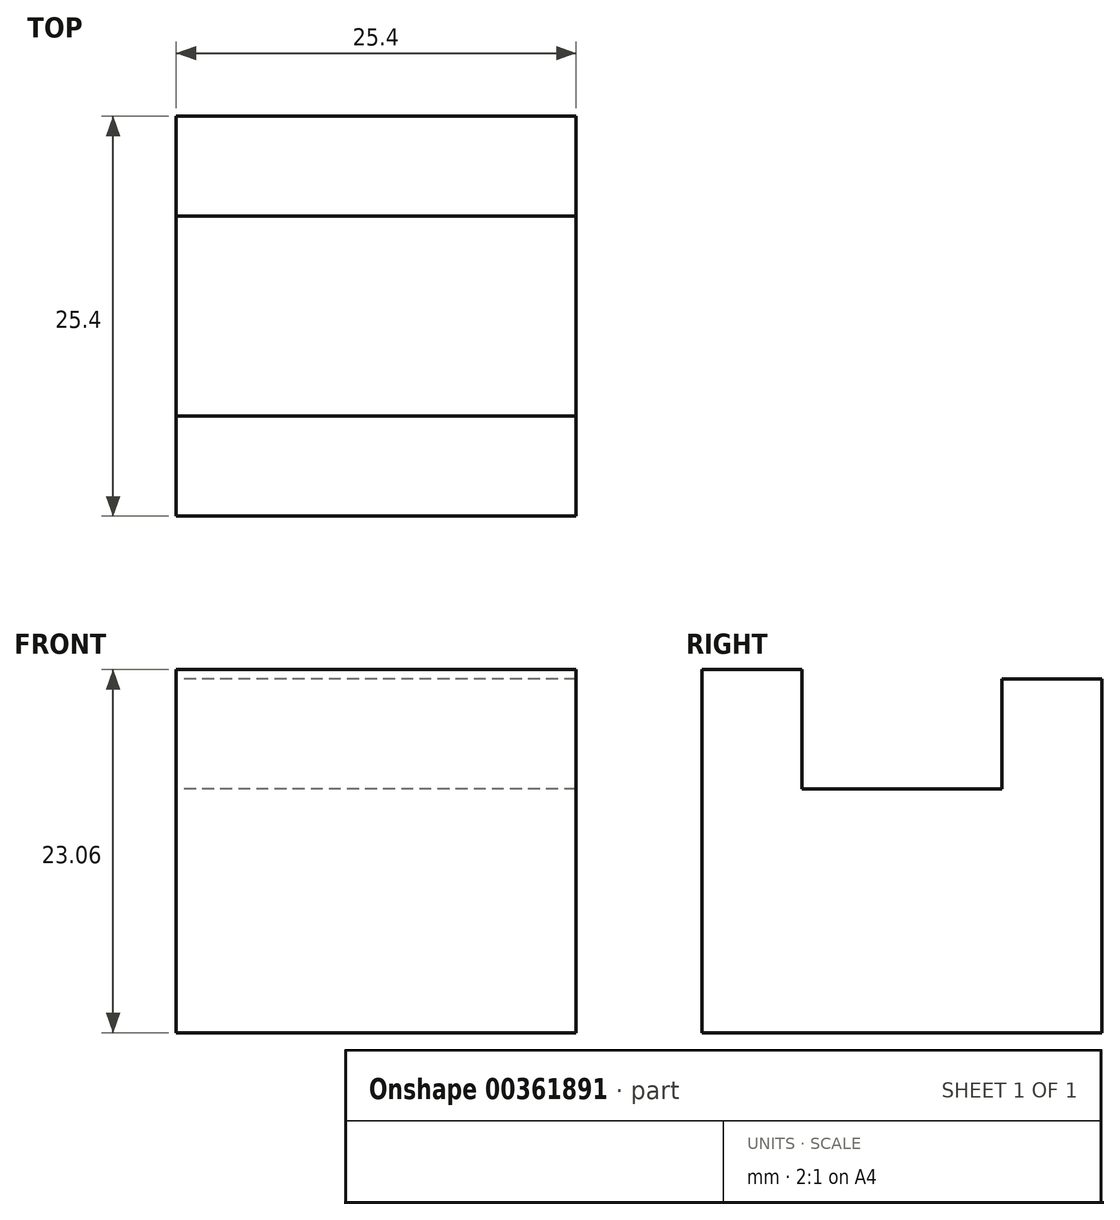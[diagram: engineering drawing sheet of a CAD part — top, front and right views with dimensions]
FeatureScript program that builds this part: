
annotation { "Feature Type Name" : "Feature", "Feature Type Description" : "" }
export const myFeature = defineFeature(function(context is Context, id is Id, definition is map)
    precondition{}
    {
        {
            var Q0;
            Q0=qCreatedBy(makeId("Right.planeOp"),FACE);
            var sketch = newSketch(context, id + "F0", { "sketchPlane" : qUnion([Q0])});
            skLineSegment(sketch, "E0", {"start": v(0, 0) * mm, "end": v(0, 23.06) * mm});
            skLineSegment(sketch, "E1", {"start": v(0, 23.06) * mm, "end": v(6.35, 23.06) * mm});
            skLineSegment(sketch, "E2", {"start": v(6.35, 23.06) * mm, "end": v(6.35, 15.47) * mm});
            skLineSegment(sketch, "E3", {"start": v(6.35, 15.47) * mm, "end": v(19.05, 15.47) * mm});
            skLineSegment(sketch, "E4", {"start": v(19.05, 15.47) * mm, "end": v(19.05, 22.48) * mm});
            skLineSegment(sketch, "E5", {"start": v(19.05, 22.48) * mm, "end": v(25.4, 22.48) * mm});
            skLineSegment(sketch, "E6", {"start": v(25.4, 22.48) * mm, "end": v(25.4, 0) * mm});
            skLineSegment(sketch, "E7", {"start": v(25.4, 0) * mm, "end": v(0, 0) * mm});
            skSolve(sketch);
        }
        {
            var Q0;
            Q0=makeQuery(id+"F0.imprint","IMPRINT",FACE,{"disambiguationData":[TD([[makeQuery(id+"F0.imprint","IMPRINT",EDGE,{"derivedFrom":sQuery(id+"F0.wireOp",EDGE,"E0")}),-1.0]])]});
            extrude(context, id + "F1", {"entities" : qUnion([Q0]), "depth" : 25.4 * mm});
        }
    });
